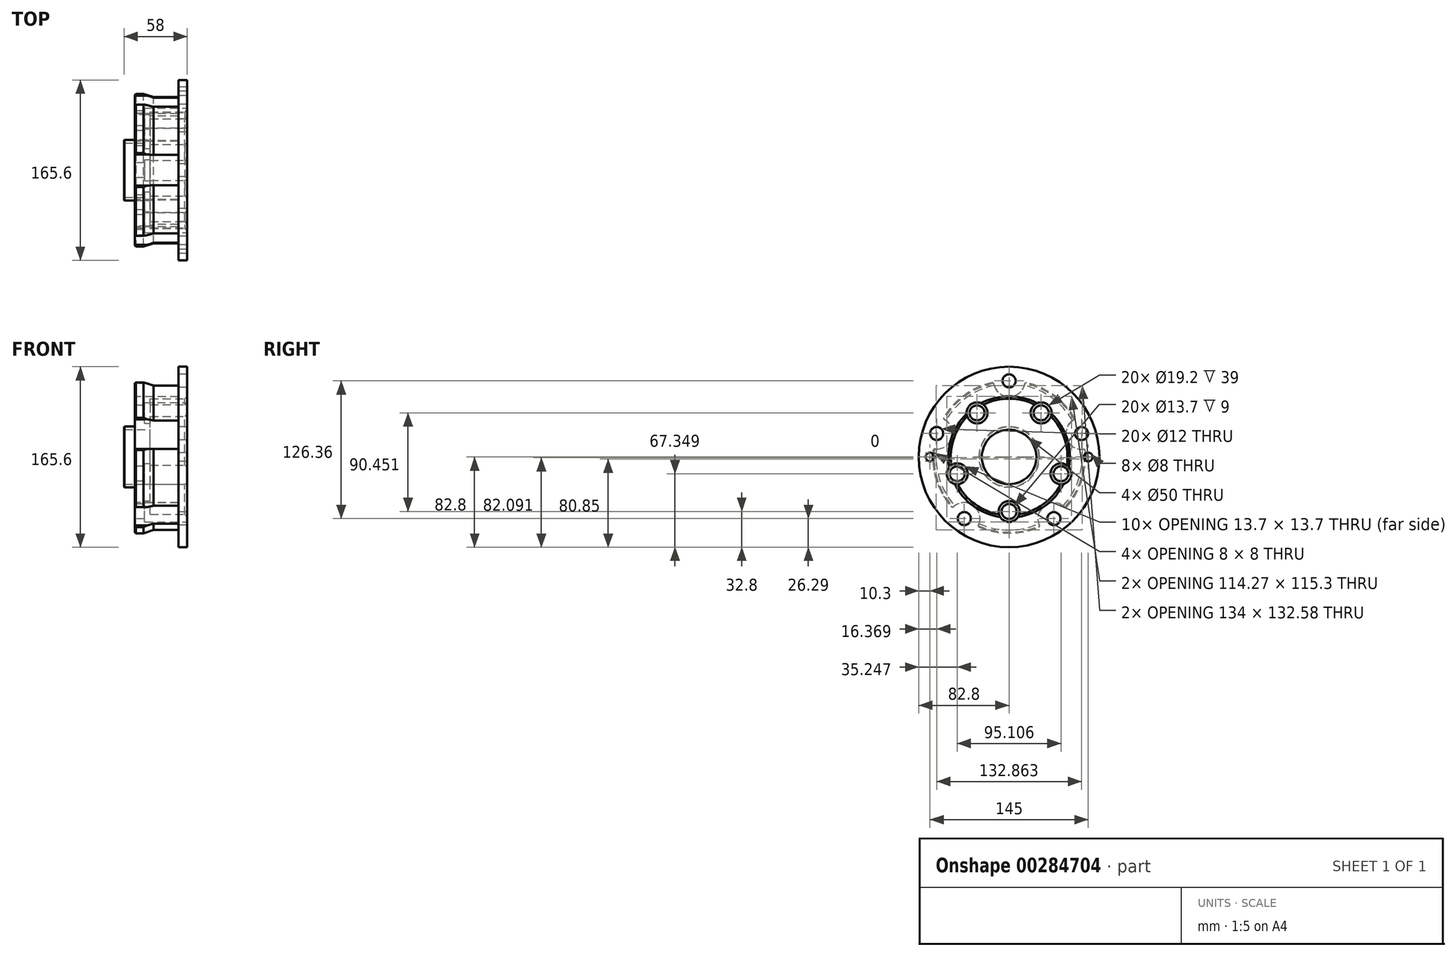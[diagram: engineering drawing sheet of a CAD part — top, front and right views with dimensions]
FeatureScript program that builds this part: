
annotation { "Feature Type Name" : "Feature", "Feature Type Description" : "" }
export const myFeature = defineFeature(function(context is Context, id is Id, definition is map)
    precondition{}
    {
        {
            var Q0;
            Q0=qCreatedBy(makeId("Front.planeOp"),FACE);
            var sketch = newSketch(context, id + "F0", { "sketchPlane" : qUnion([Q0])});
            skLineSegment(sketch, "E0", {"start": v(0, 0) * mm, "end": v(-58, 0) * mm});
            skLineSegment(sketch, "E1", {"start": v(0, 53.5) * mm, "end": v(0, 84.9) * mm});
            skLineSegment(sketch, "E2", {"start": v(0, 84.9) * mm, "end": v(-2.2, 84.9) * mm});
            skPoint(sketch, "E3", {"position": v(-2.2, 104) * mm});
            skLineSegment(sketch, "E4", {"start": v(-2.2, 84.9) * mm, "end": v(-2.2, 104) * mm});
            skLineSegment(sketch, "E5", {"start": v(-2.2, 104) * mm, "end": v(-10.2, 104) * mm});
            skPoint(sketch, "E6", {"position": v(-10.2, 67) * mm});
            skLineSegment(sketch, "E7", {"start": v(-10.2, 104) * mm, "end": v(-10.2, 67) * mm});
            skLineSegment(sketch, "E8", {"start": v(-10.2, 67) * mm, "end": v(-33.2, 67) * mm});
            skLineSegment(sketch, "E9", {"start": v(-33.2, 67) * mm, "end": v(-36.2, 67) * mm});
            skPoint(sketch, "E10", {"position": v(-50.2, 70) * mm});
            skLineSegment(sketch, "E11", {"start": v(-50.2, 70) * mm, "end": v(-50.2, 25) * mm});
            skPoint(sketch, "E12", {"position": v(0, 53.5) * mm});
            skLineSegment(sketch, "E13", {"start": v(0, 53.5) * mm, "end": v(-36.2, 53.5) * mm});
            skLineSegment(sketch, "E14", {"start": v(-36.2, 67) * mm, "end": v(-36.2, 0) * mm});
            skLineSegment(sketch, "E15", {"start": v(-36.2, 53.5) * mm, "end": v(-36.2, 25) * mm});
            skLineSegment(sketch, "E16", {"start": v(-50.2, 25) * mm, "end": v(-36.2, 25) * mm});
            skPoint(sketch, "E17.orphan", {"position": v(-36.2, 0) * mm});
            skPoint(sketch, "E18.orphan", {"position": v(-50.2, 0) * mm});
            skLineSegment(sketch, "E19", {"start": v(-50.2, 70) * mm, "end": v(-42.2, 70) * mm});
            skLineSegment(sketch, "E20", {"start": v(-42.2, 70) * mm, "end": v(-33.2, 67) * mm});
            skLineSegment(sketch, "E21", {"start": v(-2.2, 84.9) * mm, "end": v(-2.2, 53.5) * mm});
            skPoint(sketch, "E22", {"position": v(-2.2, 82.8) * mm});
            skLineSegment(sketch, "E23", {"start": v(-2.2, 82.8) * mm, "end": v(-10.2, 82.8) * mm});
            skLineSegment(sketch, "E24", {"start": v(-2.2, 82.8) * mm, "end": v(0, 82.8) * mm});
            skLineSegment(sketch, "E25", {"start": v(-50.2, 25) * mm, "end": v(-60.2, 25) * mm});
            skLineSegment(sketch, "E26", {"start": v(-60.2, 25) * mm, "end": v(-60.2, 27.85) * mm});
            skLineSegment(sketch, "E27", {"start": v(-60.2, 27.85) * mm, "end": v(-50.2, 27.85) * mm});
            skSolve(sketch);
        }
        {
            var Q0;
            Q0=qSketchRegion(id+"F0",true);
            var Q1;
            Q1=sQuery(id+"F0.wireOp",EDGE,"E0");
            revolve(context, id + "F1", {"entities" : qUnion([Q0]), "axis" : qUnion([Q1]), "revolveType" : RevolveType.FULL});
        }
        {
            var Q0;
            Q0=makeQuery(id+"F1.opRevolve","SWEPT_FACE",FACE,{"disambiguationData":[OSD([sQuery(id+"F0.wireOp",EDGE,"E11")])]});
            var sketch = newSketch(context, id + "F2", { "sketchPlane" : qUnion([Q0])});
            skCircle(sketch, "E28.0", {"center": v(0, 0) * mm, "radius": 70 * mm});
            skCircle(sketch, "E29", {"center": v(0, 0) * mm, "radius": 69.85 * mm, "construction": true});
            skLineSegment(sketch, "E30", {"start": v(0, 0) * mm, "end": v(0, 69.85) * mm});
            skCircle(sketch, "E31", {"center": v(0, 69.85) * mm, "radius": 6 * mm});
            skCircle(sketch, "E32.1.0", {"center": v(-66.43, 21.58) * mm, "radius": 6 * mm});
            skCircle(sketch, "E32.2.0", {"center": v(-41.06, -56.5) * mm, "radius": 6 * mm});
            skCircle(sketch, "E32.3.0", {"center": v(41.06, -56.5) * mm, "radius": 6 * mm});
            skCircle(sketch, "E32.4.0", {"center": v(66.43, 21.58) * mm, "radius": 6 * mm});
            skSolve(sketch);
        }
        {
            var Q0;
            {var subQ0=sQuery(id+"F2.wireOp",EDGE,"E31");var subQ1=makeQuery(id+"F1.opRevolve","SWEPT_EDGE",EDGE,{"disambiguationData":[OSD([sQuery(id+"F0.wireOp",EDGE,"E11"),sQuery(id+"F0.wireOp",EDGE,"E19")])]});var subQ2=makeQuery(id+"F2.imprint","INTERSECT",VERTEX,{"disambiguationData":[OD(0.0)],"derivedFrom":[subQ1,subQ0]});Q0=makeQuery(id+"F2.imprint","IMPRINT",FACE,{"disambiguationData":[TD([[makeQuery(id+"F2.imprint","IMPRINT",EDGE,{"disambiguationData":[TD([[subQ2,-1.0]])],"derivedFrom":subQ0}),1.0]])]});}
            var Q1;
            {var subQ0=sQuery(id+"F2.wireOp",EDGE,"E31");var subQ1=makeQuery(id+"F1.opRevolve","SWEPT_EDGE",EDGE,{"disambiguationData":[OSD([sQuery(id+"F0.wireOp",EDGE,"E11"),sQuery(id+"F0.wireOp",EDGE,"E19")])]});var subQ2=makeQuery(id+"F2.imprint","INTERSECT",VERTEX,{"disambiguationData":[OD(0.0)],"derivedFrom":[subQ1,subQ0]});Q1=makeQuery(id+"F2.imprint","IMPRINT",FACE,{"disambiguationData":[TD([[makeQuery(id+"F2.imprint","IMPRINT",EDGE,{"disambiguationData":[TD([[subQ2,1.0]])],"derivedFrom":subQ0}),1.0]])]});}
            var Q2;
            {var subQ0=sQuery(id+"F2.wireOp",EDGE,"E32.4.0");var subQ1=makeQuery(id+"F1.opRevolve","SWEPT_EDGE",EDGE,{"disambiguationData":[OSD([sQuery(id+"F0.wireOp",EDGE,"E11"),sQuery(id+"F0.wireOp",EDGE,"E19")])]});var subQ2=makeQuery(id+"F2.imprint","INTERSECT",VERTEX,{"disambiguationData":[OD(0.0)],"derivedFrom":[subQ1,subQ0]});Q2=makeQuery(id+"F2.imprint","IMPRINT",FACE,{"disambiguationData":[TD([[makeQuery(id+"F2.imprint","IMPRINT",EDGE,{"disambiguationData":[TD([[subQ2,-1.0]])],"derivedFrom":subQ0}),1.0]])]});}
            var Q3;
            {var subQ0=sQuery(id+"F2.wireOp",EDGE,"E32.4.0");var subQ1=makeQuery(id+"F1.opRevolve","SWEPT_EDGE",EDGE,{"disambiguationData":[OSD([sQuery(id+"F0.wireOp",EDGE,"E11"),sQuery(id+"F0.wireOp",EDGE,"E19")])]});var subQ2=makeQuery(id+"F2.imprint","INTERSECT",VERTEX,{"disambiguationData":[OD(0.0)],"derivedFrom":[subQ1,subQ0]});Q3=makeQuery(id+"F2.imprint","IMPRINT",FACE,{"disambiguationData":[TD([[makeQuery(id+"F2.imprint","IMPRINT",EDGE,{"disambiguationData":[TD([[subQ2,1.0]])],"derivedFrom":subQ0}),1.0]])]});}
            var Q4;
            {var subQ0=sQuery(id+"F2.wireOp",EDGE,"E32.3.0");var subQ1=makeQuery(id+"F1.opRevolve","SWEPT_EDGE",EDGE,{"disambiguationData":[OSD([sQuery(id+"F0.wireOp",EDGE,"E11"),sQuery(id+"F0.wireOp",EDGE,"E19")])]});var subQ2=makeQuery(id+"F2.imprint","INTERSECT",VERTEX,{"disambiguationData":[OD(0.0)],"derivedFrom":[subQ1,subQ0]});Q4=makeQuery(id+"F2.imprint","IMPRINT",FACE,{"disambiguationData":[TD([[makeQuery(id+"F2.imprint","IMPRINT",EDGE,{"disambiguationData":[TD([[subQ2,1.0]])],"derivedFrom":subQ0}),1.0]])]});}
            var Q5;
            {var subQ0=sQuery(id+"F2.wireOp",EDGE,"E32.3.0");var subQ1=makeQuery(id+"F1.opRevolve","SWEPT_EDGE",EDGE,{"disambiguationData":[OSD([sQuery(id+"F0.wireOp",EDGE,"E11"),sQuery(id+"F0.wireOp",EDGE,"E19")])]});var subQ2=makeQuery(id+"F2.imprint","INTERSECT",VERTEX,{"disambiguationData":[OD(0.0)],"derivedFrom":[subQ1,subQ0]});Q5=makeQuery(id+"F2.imprint","IMPRINT",FACE,{"disambiguationData":[TD([[makeQuery(id+"F2.imprint","IMPRINT",EDGE,{"disambiguationData":[TD([[subQ2,-1.0]])],"derivedFrom":subQ0}),1.0]])]});}
            var Q6;
            {var subQ0=sQuery(id+"F2.wireOp",EDGE,"E32.2.0");var subQ1=makeQuery(id+"F1.opRevolve","SWEPT_EDGE",EDGE,{"disambiguationData":[OSD([sQuery(id+"F0.wireOp",EDGE,"E11"),sQuery(id+"F0.wireOp",EDGE,"E19")])]});var subQ2=makeQuery(id+"F2.imprint","INTERSECT",VERTEX,{"disambiguationData":[OD(0.0)],"derivedFrom":[subQ1,subQ0]});Q6=makeQuery(id+"F2.imprint","IMPRINT",FACE,{"disambiguationData":[TD([[makeQuery(id+"F2.imprint","IMPRINT",EDGE,{"disambiguationData":[TD([[subQ2,1.0]])],"derivedFrom":subQ0}),1.0]])]});}
            var Q7;
            {var subQ0=sQuery(id+"F2.wireOp",EDGE,"E32.2.0");var subQ1=makeQuery(id+"F1.opRevolve","SWEPT_EDGE",EDGE,{"disambiguationData":[OSD([sQuery(id+"F0.wireOp",EDGE,"E11"),sQuery(id+"F0.wireOp",EDGE,"E19")])]});var subQ2=makeQuery(id+"F2.imprint","INTERSECT",VERTEX,{"disambiguationData":[OD(0.0)],"derivedFrom":[subQ1,subQ0]});Q7=makeQuery(id+"F2.imprint","IMPRINT",FACE,{"disambiguationData":[TD([[makeQuery(id+"F2.imprint","IMPRINT",EDGE,{"disambiguationData":[TD([[subQ2,-1.0]])],"derivedFrom":subQ0}),1.0]])]});}
            var Q8;
            {var subQ0=sQuery(id+"F2.wireOp",EDGE,"E32.1.0");var subQ1=makeQuery(id+"F1.opRevolve","SWEPT_EDGE",EDGE,{"disambiguationData":[OSD([sQuery(id+"F0.wireOp",EDGE,"E11"),sQuery(id+"F0.wireOp",EDGE,"E19")])]});var subQ2=makeQuery(id+"F2.imprint","INTERSECT",VERTEX,{"disambiguationData":[OD(0.0)],"derivedFrom":[subQ1,subQ0]});Q8=makeQuery(id+"F2.imprint","IMPRINT",FACE,{"disambiguationData":[TD([[makeQuery(id+"F2.imprint","IMPRINT",EDGE,{"disambiguationData":[TD([[subQ2,-1.0]])],"derivedFrom":subQ0}),1.0]])]});}
            var Q9;
            {var subQ0=sQuery(id+"F2.wireOp",EDGE,"E32.1.0");var subQ1=makeQuery(id+"F1.opRevolve","SWEPT_EDGE",EDGE,{"disambiguationData":[OSD([sQuery(id+"F0.wireOp",EDGE,"E11"),sQuery(id+"F0.wireOp",EDGE,"E19")])]});var subQ2=makeQuery(id+"F2.imprint","INTERSECT",VERTEX,{"disambiguationData":[OD(0.0)],"derivedFrom":[subQ1,subQ0]});Q9=makeQuery(id+"F2.imprint","IMPRINT",FACE,{"disambiguationData":[TD([[makeQuery(id+"F2.imprint","IMPRINT",EDGE,{"disambiguationData":[TD([[subQ2,1.0]])],"derivedFrom":subQ0}),1.0]])]});}
            extrude(context, id + "F3", {"entities" : qUnion([Q0, Q1, Q2, Q3, Q4, Q5, Q6, Q7, Q8, Q9]), "operationType" : NewBodyOperationType.REMOVE, "oppositeDirection" : true, "depth" : 48 * mm});
        }
        {
            var Q0;
            Q0=makeQuery(id+"F1.opRevolve","SWEPT_FACE",FACE,{"disambiguationData":[OSD([sQuery(id+"F0.wireOp",EDGE,"E11")])]});
            var sketch = newSketch(context, id + "F4", { "sketchPlane" : qUnion([Q0])});
            skCircle(sketch, "E33.0", {"center": v(0, 0) * mm, "radius": 25 * mm, "construction": true});
            skCircle(sketch, "E34", {"center": v(0, 0) * mm, "radius": 69.85 * mm, "construction": true});
            skPoint(sketch, "E35", {"position": v(-0.15, 69.85) * mm});
            skCircle(sketch, "E36", {"center": v(-0.15, 69.85) * mm, "radius": 14.5 * mm});
            skCircle(sketch, "E37.1.0", {"center": v(-66.48, 21.45) * mm, "radius": 14.5 * mm});
            skCircle(sketch, "E37.2.0", {"center": v(-40.94, -56.6) * mm, "radius": 14.5 * mm});
            skCircle(sketch, "E37.3.0", {"center": v(41.17, -56.42) * mm, "radius": 14.5 * mm});
            skCircle(sketch, "E37.4.0", {"center": v(66.39, 21.72) * mm, "radius": 14.5 * mm});
            skSolve(sketch);
        }
        {
            var Q0;
            Q0=qSketchRegion(id+"F4",true);
            extrude(context, id + "F5", {"entities" : qUnion([Q0]), "operationType" : NewBodyOperationType.REMOVE, "oppositeDirection" : true, "depth" : 40 * mm});
        }
        {
            var Q0;
            Q0=makeQuery(id+"F1.opRevolve","SWEPT_FACE",FACE,{"disambiguationData":[OSD([sQuery(id+"F0.wireOp",EDGE,"E11")])]});
            var sketch = newSketch(context, id + "F6", { "sketchPlane" : qUnion([Q0])});
            skCircle(sketch, "E38", {"center": v(0, 0) * mm, "radius": 50 * mm, "construction": true});
            skLineSegment(sketch, "E39", {"start": v(0, 0) * mm, "end": v(-29.39, 40.45) * mm});
            skCircle(sketch, "E40", {"center": v(-29.39, 40.45) * mm, "radius": 6.85 * mm});
            skCircle(sketch, "E41.1.0", {"center": v(-47.55, -15.45) * mm, "radius": 6.85 * mm});
            skCircle(sketch, "E41.2.0", {"center": v(0, -50) * mm, "radius": 6.85 * mm});
            skCircle(sketch, "E41.3.0", {"center": v(47.55, -15.45) * mm, "radius": 6.85 * mm});
            skCircle(sketch, "E41.4.0", {"center": v(29.39, 40.45) * mm, "radius": 6.85 * mm});
            skSolve(sketch);
        }
        {
            var Q0;
            Q0=qSketchRegion(id+"F6",true);
            extrude(context, id + "F7", {"entities" : qUnion([Q0]), "operationType" : NewBodyOperationType.REMOVE, "oppositeDirection" : true, "depth" : 14 * mm});
        }
        {
            var Q0;
            Q0=makeQuery(id+"F1.opRevolve","SWEPT_FACE",FACE,{"disambiguationData":[OSD([sQuery(id+"F0.wireOp",EDGE,"E1")])]});
            var sketch = newSketch(context, id + "F8", { "sketchPlane" : qUnion([Q0])});
            skCircle(sketch, "E42", {"center": v(0, 0) * mm, "radius": 50 * mm, "construction": true});
            skArc(sketch, "E43.0", {"start": v(-26.32, 46.58) * mm, "mid": v(-25.36, 34.9) * mm, "end": v(-36.16, 39.43) * mm, "construction": true});
            skCircle(sketch, "E44", {"center": v(-29.39, 40.45) * mm, "radius": 9.6 * mm});
            skCircle(sketch, "E45.1.0", {"center": v(-47.55, -15.45) * mm, "radius": 9.6 * mm});
            skCircle(sketch, "E45.2.0", {"center": v(0, -50) * mm, "radius": 9.6 * mm});
            skCircle(sketch, "E45.3.0", {"center": v(47.55, -15.45) * mm, "radius": 9.6 * mm});
            skCircle(sketch, "E45.4.0", {"center": v(29.39, 40.45) * mm, "radius": 9.6 * mm});
            skSolve(sketch);
        }
        {
            var Q0;
            Q0=qSketchRegion(id+"F8",true);
            extrude(context, id + "F9", {"entities" : qUnion([Q0]), "operationType" : NewBodyOperationType.REMOVE, "oppositeDirection" : true, "depth" : 41.2 * mm});
        }
        {
            var Q0;
            Q0=makeQuery(id+"F5.boolean.opBoolean","MERGE",FACE,{"derivedFrom":[makeQuery(id+"F1.opRevolve","SWEPT_FACE",FACE,{"disambiguationData":[OSD([sQuery(id+"F0.wireOp",EDGE,"E7")])]}),makeQuery(id+"F5.opExtrude","CAP_FACE",FACE,{"disambiguationData":[OSD([sQuery(id+"F4.wireOp",EDGE,"E36")])],"isStart":false}),makeQuery(id+"F5.opExtrude","CAP_FACE",FACE,{"disambiguationData":[OSD([sQuery(id+"F4.wireOp",EDGE,"E37.1.0")])],"isStart":false}),makeQuery(id+"F5.opExtrude","CAP_FACE",FACE,{"disambiguationData":[OSD([sQuery(id+"F4.wireOp",EDGE,"E37.2.0")])],"isStart":false}),makeQuery(id+"F5.opExtrude","CAP_FACE",FACE,{"disambiguationData":[OSD([sQuery(id+"F4.wireOp",EDGE,"E37.3.0")])],"isStart":false}),makeQuery(id+"F5.opExtrude","CAP_FACE",FACE,{"disambiguationData":[OSD([sQuery(id+"F4.wireOp",EDGE,"E37.4.0")])],"isStart":false})]});
            var sketch = newSketch(context, id + "F10", { "sketchPlane" : qUnion([Q0])});
            skLineSegment(sketch, "E46", {"start": v(0, 0) * mm, "end": v(-29.36, 90.35) * mm});
            skCircle(sketch, "E47", {"center": v(0, 0) * mm, "radius": 95 * mm, "construction": true});
            skCircle(sketch, "E48", {"center": v(-29.36, 90.35) * mm, "radius": 4 * mm});
            skCircle(sketch, "E49.1.0", {"center": v(-76.86, 55.84) * mm, "radius": 4 * mm});
            skCircle(sketch, "E49.2.0", {"center": v(-95, 0) * mm, "radius": 4 * mm});
            skCircle(sketch, "E49.3.0", {"center": v(-76.86, -55.84) * mm, "radius": 4 * mm});
            skCircle(sketch, "E49.4.0", {"center": v(-29.36, -90.35) * mm, "radius": 4 * mm});
            skCircle(sketch, "E49.5.0", {"center": v(29.36, -90.35) * mm, "radius": 4 * mm});
            skCircle(sketch, "E49.6.0", {"center": v(76.86, -55.84) * mm, "radius": 4 * mm});
            skCircle(sketch, "E49.7.0", {"center": v(95, 0) * mm, "radius": 4 * mm});
            skCircle(sketch, "E49.8.0", {"center": v(76.86, 55.84) * mm, "radius": 4 * mm});
            skCircle(sketch, "E49.9.0", {"center": v(29.36, 90.35) * mm, "radius": 4 * mm});
            skSolve(sketch);
        }
        {
            var Q0;
            Q0=qSketchRegion(id+"F10",true);
            extrude(context, id + "F11", {"entities" : qUnion([Q0]), "operationType" : NewBodyOperationType.REMOVE, "oppositeDirection" : true, "depth" : 8 * mm});
        }
        {
            var Q0;
            Q0=makeQuery(id+"F5.boolean.opBoolean","MERGE",FACE,{"derivedFrom":[makeQuery(id+"F1.opRevolve","SWEPT_FACE",FACE,{"disambiguationData":[OSD([sQuery(id+"F0.wireOp",EDGE,"E7")])]}),makeQuery(id+"F5.opExtrude","CAP_FACE",FACE,{"disambiguationData":[OSD([sQuery(id+"F4.wireOp",EDGE,"E36")])],"isStart":false}),makeQuery(id+"F5.opExtrude","CAP_FACE",FACE,{"disambiguationData":[OSD([sQuery(id+"F4.wireOp",EDGE,"E37.1.0")])],"isStart":false}),makeQuery(id+"F5.opExtrude","CAP_FACE",FACE,{"disambiguationData":[OSD([sQuery(id+"F4.wireOp",EDGE,"E37.2.0")])],"isStart":false}),makeQuery(id+"F5.opExtrude","CAP_FACE",FACE,{"disambiguationData":[OSD([sQuery(id+"F4.wireOp",EDGE,"E37.3.0")])],"isStart":false}),makeQuery(id+"F5.opExtrude","CAP_FACE",FACE,{"disambiguationData":[OSD([sQuery(id+"F4.wireOp",EDGE,"E37.4.0")])],"isStart":false})]});
            var sketch = newSketch(context, id + "F12", { "sketchPlane" : qUnion([Q0])});
            skCircle(sketch, "E50", {"center": v(0, 0) * mm, "radius": 95 * mm, "construction": true});
            skCircle(sketch, "E51.0", {"center": v(-29.36, 90.35) * mm, "radius": 4 * mm, "construction": true});
            skCircle(sketch, "E52", {"center": v(-29.36, 90.35) * mm, "radius": 7 * mm});
            skCircle(sketch, "E53.1.0", {"center": v(-76.86, 55.84) * mm, "radius": 7 * mm});
            skCircle(sketch, "E53.2.0", {"center": v(-95, 0) * mm, "radius": 7 * mm});
            skCircle(sketch, "E53.3.0", {"center": v(-76.86, -55.84) * mm, "radius": 7 * mm});
            skCircle(sketch, "E53.4.0", {"center": v(-29.36, -90.35) * mm, "radius": 7 * mm});
            skCircle(sketch, "E53.5.0", {"center": v(29.36, -90.35) * mm, "radius": 7 * mm});
            skCircle(sketch, "E53.6.0", {"center": v(76.86, -55.84) * mm, "radius": 7 * mm});
            skCircle(sketch, "E53.7.0", {"center": v(95, 0) * mm, "radius": 7 * mm});
            skCircle(sketch, "E53.8.0", {"center": v(76.86, 55.84) * mm, "radius": 7 * mm});
            skCircle(sketch, "E53.9.0", {"center": v(29.36, 90.35) * mm, "radius": 7 * mm});
            skSolve(sketch);
        }
        {
            var Q0;
            Q0=qSketchRegion(id+"F12",true);
            extrude(context, id + "F13", {"entities" : qUnion([Q0]), "operationType" : NewBodyOperationType.REMOVE, "oppositeDirection" : true, "depth" : 1 * mm});
        }
        {
            var Q0;
            {var subQ0=sQuery(id+"F0.wireOp",EDGE,"E1");var subQ1=sQuery(id+"F0.wireOp",EDGE,"E13");Q0=makeQuery(id+"F9.boolean.opBoolean","SPLIT",EDGE,{"disambiguationData":[TD([makeQuery(id+"F1.opRevolve","SWEPT_FACE",FACE,{"disambiguationData":[OSD([subQ0])]}),makeQuery(id+"F1.opRevolve","SWEPT_FACE",FACE,{"disambiguationData":[OSD([subQ1])]}),makeQuery(id+"F9.opExtrude","SWEPT_FACE",FACE,{"disambiguationData":[OSD([sQuery(id+"F8.wireOp",EDGE,"E44")])]}),makeQuery(id+"F9.opExtrude","SWEPT_FACE",FACE,{"disambiguationData":[OSD([sQuery(id+"F8.wireOp",EDGE,"E45.4.0")])]})])],"derivedFrom":makeQuery(id+"F1.opRevolve","SWEPT_EDGE",EDGE,{"disambiguationData":[OSD([subQ0,subQ1])]})});}
            var Q1;
            {var subQ0=sQuery(id+"F0.wireOp",EDGE,"E1");var subQ1=sQuery(id+"F0.wireOp",EDGE,"E13");Q1=makeQuery(id+"F9.boolean.opBoolean","SPLIT",EDGE,{"disambiguationData":[TD([makeQuery(id+"F1.opRevolve","SWEPT_FACE",FACE,{"disambiguationData":[OSD([subQ0])]}),makeQuery(id+"F1.opRevolve","SWEPT_FACE",FACE,{"disambiguationData":[OSD([subQ1])]}),makeQuery(id+"F9.opExtrude","SWEPT_FACE",FACE,{"disambiguationData":[OSD([sQuery(id+"F8.wireOp",EDGE,"E45.3.0")])]}),makeQuery(id+"F9.opExtrude","SWEPT_FACE",FACE,{"disambiguationData":[OSD([sQuery(id+"F8.wireOp",EDGE,"E45.4.0")])]})])],"derivedFrom":makeQuery(id+"F1.opRevolve","SWEPT_EDGE",EDGE,{"disambiguationData":[OSD([subQ0,subQ1])]})});}
            var Q2;
            {var subQ0=sQuery(id+"F0.wireOp",EDGE,"E1");var subQ1=sQuery(id+"F0.wireOp",EDGE,"E13");Q2=makeQuery(id+"F9.boolean.opBoolean","SPLIT",EDGE,{"disambiguationData":[TD([makeQuery(id+"F1.opRevolve","SWEPT_FACE",FACE,{"disambiguationData":[OSD([subQ0])]}),makeQuery(id+"F1.opRevolve","SWEPT_FACE",FACE,{"disambiguationData":[OSD([subQ1])]}),makeQuery(id+"F9.opExtrude","SWEPT_FACE",FACE,{"disambiguationData":[OSD([sQuery(id+"F8.wireOp",EDGE,"E45.2.0")])]}),makeQuery(id+"F9.opExtrude","SWEPT_FACE",FACE,{"disambiguationData":[OSD([sQuery(id+"F8.wireOp",EDGE,"E45.3.0")])]})])],"derivedFrom":makeQuery(id+"F1.opRevolve","SWEPT_EDGE",EDGE,{"disambiguationData":[OSD([subQ0,subQ1])]})});}
            var Q3;
            {var subQ0=sQuery(id+"F0.wireOp",EDGE,"E1");var subQ1=sQuery(id+"F0.wireOp",EDGE,"E13");Q3=makeQuery(id+"F9.boolean.opBoolean","SPLIT",EDGE,{"disambiguationData":[TD([makeQuery(id+"F1.opRevolve","SWEPT_FACE",FACE,{"disambiguationData":[OSD([subQ0])]}),makeQuery(id+"F1.opRevolve","SWEPT_FACE",FACE,{"disambiguationData":[OSD([subQ1])]}),makeQuery(id+"F9.opExtrude","SWEPT_FACE",FACE,{"disambiguationData":[OSD([sQuery(id+"F8.wireOp",EDGE,"E45.1.0")])]}),makeQuery(id+"F9.opExtrude","SWEPT_FACE",FACE,{"disambiguationData":[OSD([sQuery(id+"F8.wireOp",EDGE,"E45.2.0")])]})])],"derivedFrom":makeQuery(id+"F1.opRevolve","SWEPT_EDGE",EDGE,{"disambiguationData":[OSD([subQ0,subQ1])]})});}
            var Q4;
            {var subQ0=sQuery(id+"F0.wireOp",EDGE,"E1");var subQ1=sQuery(id+"F0.wireOp",EDGE,"E13");Q4=makeQuery(id+"F9.boolean.opBoolean","SPLIT",EDGE,{"disambiguationData":[TD([makeQuery(id+"F1.opRevolve","SWEPT_FACE",FACE,{"disambiguationData":[OSD([subQ0])]}),makeQuery(id+"F1.opRevolve","SWEPT_FACE",FACE,{"disambiguationData":[OSD([subQ1])]}),makeQuery(id+"F9.opExtrude","SWEPT_FACE",FACE,{"disambiguationData":[OSD([sQuery(id+"F8.wireOp",EDGE,"E44")])]}),makeQuery(id+"F9.opExtrude","SWEPT_FACE",FACE,{"disambiguationData":[OSD([sQuery(id+"F8.wireOp",EDGE,"E45.1.0")])]})])],"derivedFrom":makeQuery(id+"F1.opRevolve","SWEPT_EDGE",EDGE,{"disambiguationData":[OSD([subQ0,subQ1])]})});}
            chamfer(context, id + "F14", {"entities" : qUnion([Q0, Q1, Q2, Q3, Q4]), "width" : 2.2 * mm, "tangentPropagation" : true});
        }
        {
            var Q0;
            {var subQ0=sQuery(id+"F0.wireOp",EDGE,"E11");var subQ1=sQuery(id+"F0.wireOp",EDGE,"E19");Q0=makeQuery(id+"F3.boolean.opBoolean","SPLIT",EDGE,{"disambiguationData":[TD([makeQuery(id+"F1.opRevolve","SWEPT_FACE",FACE,{"disambiguationData":[OSD([subQ0])]}),makeQuery(id+"F1.opRevolve","SWEPT_FACE",FACE,{"disambiguationData":[OSD([subQ1])]}),makeQuery(id+"F3.opExtrude","SWEPT_FACE",FACE,{"disambiguationData":[OSD([sQuery(id+"F2.wireOp",EDGE,"isoNOGXv-9rzR-vXjO-d8jj-fEhT8795Os4k")])]}),makeQuery(id+"F3.opExtrude","SWEPT_FACE",FACE,{"disambiguationData":[OSD([sQuery(id+"F2.wireOp",EDGE,"ed49934d-06d9-406b-9f25-b05f826b0471.4.0")])]})])],"derivedFrom":makeQuery(id+"F1.opRevolve","SWEPT_EDGE",EDGE,{"disambiguationData":[OSD([subQ0,subQ1])]})});}
            var Q1;
            Q1=makeQuery(id+"F5.boolean.opBoolean","COPY",EDGE,{"derivedFrom":makeQuery(id+"F5.opExtrude","CAP_EDGE",EDGE,{"disambiguationData":[OSD([sQuery(id+"F4.wireOp",EDGE,"E37.4.0")])],"isStart":true})});
            var Q2;
            {var subQ0=sQuery(id+"F0.wireOp",EDGE,"E11");var subQ1=sQuery(id+"F0.wireOp",EDGE,"E19");Q2=makeQuery(id+"F3.boolean.opBoolean","SPLIT",EDGE,{"disambiguationData":[TD([makeQuery(id+"F1.opRevolve","SWEPT_FACE",FACE,{"disambiguationData":[OSD([subQ0])]}),makeQuery(id+"F1.opRevolve","SWEPT_FACE",FACE,{"disambiguationData":[OSD([subQ1])]}),makeQuery(id+"F3.opExtrude","SWEPT_FACE",FACE,{"disambiguationData":[OSD([sQuery(id+"F2.wireOp",EDGE,"ed49934d-06d9-406b-9f25-b05f826b0471.3.0")])]}),makeQuery(id+"F3.opExtrude","SWEPT_FACE",FACE,{"disambiguationData":[OSD([sQuery(id+"F2.wireOp",EDGE,"ed49934d-06d9-406b-9f25-b05f826b0471.4.0")])]})])],"derivedFrom":makeQuery(id+"F1.opRevolve","SWEPT_EDGE",EDGE,{"disambiguationData":[OSD([subQ0,subQ1])]})});}
            var Q3;
            Q3=makeQuery(id+"F5.boolean.opBoolean","COPY",EDGE,{"derivedFrom":makeQuery(id+"F5.opExtrude","CAP_EDGE",EDGE,{"disambiguationData":[OSD([sQuery(id+"F4.wireOp",EDGE,"E37.3.0")])],"isStart":true})});
            var Q4;
            {var subQ0=sQuery(id+"F0.wireOp",EDGE,"E11");var subQ1=sQuery(id+"F0.wireOp",EDGE,"E19");Q4=makeQuery(id+"F3.boolean.opBoolean","SPLIT",EDGE,{"disambiguationData":[TD([makeQuery(id+"F1.opRevolve","SWEPT_FACE",FACE,{"disambiguationData":[OSD([subQ0])]}),makeQuery(id+"F1.opRevolve","SWEPT_FACE",FACE,{"disambiguationData":[OSD([subQ1])]}),makeQuery(id+"F3.opExtrude","SWEPT_FACE",FACE,{"disambiguationData":[OSD([sQuery(id+"F2.wireOp",EDGE,"ed49934d-06d9-406b-9f25-b05f826b0471.2.0")])]}),makeQuery(id+"F3.opExtrude","SWEPT_FACE",FACE,{"disambiguationData":[OSD([sQuery(id+"F2.wireOp",EDGE,"ed49934d-06d9-406b-9f25-b05f826b0471.3.0")])]})])],"derivedFrom":makeQuery(id+"F1.opRevolve","SWEPT_EDGE",EDGE,{"disambiguationData":[OSD([subQ0,subQ1])]})});}
            var Q5;
            Q5=makeQuery(id+"F5.boolean.opBoolean","COPY",EDGE,{"derivedFrom":makeQuery(id+"F5.opExtrude","CAP_EDGE",EDGE,{"disambiguationData":[OSD([sQuery(id+"F4.wireOp",EDGE,"E37.2.0")])],"isStart":true})});
            var Q6;
            {var subQ0=sQuery(id+"F0.wireOp",EDGE,"E11");var subQ1=sQuery(id+"F0.wireOp",EDGE,"E19");Q6=makeQuery(id+"F3.boolean.opBoolean","SPLIT",EDGE,{"disambiguationData":[TD([makeQuery(id+"F1.opRevolve","SWEPT_FACE",FACE,{"disambiguationData":[OSD([subQ0])]}),makeQuery(id+"F1.opRevolve","SWEPT_FACE",FACE,{"disambiguationData":[OSD([subQ1])]}),makeQuery(id+"F3.opExtrude","SWEPT_FACE",FACE,{"disambiguationData":[OSD([sQuery(id+"F2.wireOp",EDGE,"ed49934d-06d9-406b-9f25-b05f826b0471.1.0")])]}),makeQuery(id+"F3.opExtrude","SWEPT_FACE",FACE,{"disambiguationData":[OSD([sQuery(id+"F2.wireOp",EDGE,"ed49934d-06d9-406b-9f25-b05f826b0471.2.0")])]})])],"derivedFrom":makeQuery(id+"F1.opRevolve","SWEPT_EDGE",EDGE,{"disambiguationData":[OSD([subQ0,subQ1])]})});}
            var Q7;
            Q7=makeQuery(id+"F5.boolean.opBoolean","COPY",EDGE,{"derivedFrom":makeQuery(id+"F5.opExtrude","CAP_EDGE",EDGE,{"disambiguationData":[OSD([sQuery(id+"F4.wireOp",EDGE,"E37.1.0")])],"isStart":true})});
            var Q8;
            {var subQ0=sQuery(id+"F0.wireOp",EDGE,"E11");var subQ1=sQuery(id+"F0.wireOp",EDGE,"E19");Q8=makeQuery(id+"F3.boolean.opBoolean","SPLIT",EDGE,{"disambiguationData":[TD([makeQuery(id+"F1.opRevolve","SWEPT_FACE",FACE,{"disambiguationData":[OSD([subQ0])]}),makeQuery(id+"F1.opRevolve","SWEPT_FACE",FACE,{"disambiguationData":[OSD([subQ1])]}),makeQuery(id+"F3.opExtrude","SWEPT_FACE",FACE,{"disambiguationData":[OSD([sQuery(id+"F2.wireOp",EDGE,"isoNOGXv-9rzR-vXjO-d8jj-fEhT8795Os4k")])]}),makeQuery(id+"F3.opExtrude","SWEPT_FACE",FACE,{"disambiguationData":[OSD([sQuery(id+"F2.wireOp",EDGE,"ed49934d-06d9-406b-9f25-b05f826b0471.1.0")])]})])],"derivedFrom":makeQuery(id+"F1.opRevolve","SWEPT_EDGE",EDGE,{"disambiguationData":[OSD([subQ0,subQ1])]})});}
            var Q9;
            Q9=makeQuery(id+"F5.boolean.opBoolean","COPY",EDGE,{"derivedFrom":makeQuery(id+"F5.opExtrude","CAP_EDGE",EDGE,{"disambiguationData":[OSD([sQuery(id+"F4.wireOp",EDGE,"E36")])],"isStart":true})});
            var Q10;
            Q10=makeQuery(id+"F5.boolean.opBoolean","INTERSECT",EDGE,{"derivedFrom":[makeQuery(id+"F3.boolean.opBoolean","SPLIT",FACE,{"disambiguationData":[TD([makeQuery(id+"F1.opRevolve","SWEPT_FACE",FACE,{"disambiguationData":[OSD([sQuery(id+"F0.wireOp",EDGE,"E11")])]}),makeQuery(id+"F1.opRevolve","SWEPT_FACE",FACE,{"disambiguationData":[OSD([sQuery(id+"F0.wireOp",EDGE,"E20")])]}),makeQuery(id+"F3.opExtrude","SWEPT_FACE",FACE,{"disambiguationData":[OSD([sQuery(id+"F2.wireOp",EDGE,"isoNOGXv-9rzR-vXjO-d8jj-fEhT8795Os4k")])]}),makeQuery(id+"F3.opExtrude","SWEPT_FACE",FACE,{"disambiguationData":[OSD([sQuery(id+"F2.wireOp",EDGE,"ed49934d-06d9-406b-9f25-b05f826b0471.4.0")])]})])],"derivedFrom":makeQuery(id+"F1.opRevolve","SWEPT_FACE",FACE,{"disambiguationData":[OSD([sQuery(id+"F0.wireOp",EDGE,"E19")])]})}),makeQuery(id+"F5.opExtrude","SWEPT_FACE",FACE,{"disambiguationData":[OSD([sQuery(id+"F4.wireOp",EDGE,"E36")])]})]});
            var Q11;
            Q11=makeQuery(id+"F5.boolean.opBoolean","INTERSECT",EDGE,{"derivedFrom":[makeQuery(id+"F3.boolean.opBoolean","SPLIT",FACE,{"disambiguationData":[TD([makeQuery(id+"F1.opRevolve","SWEPT_FACE",FACE,{"disambiguationData":[OSD([sQuery(id+"F0.wireOp",EDGE,"E11")])]}),makeQuery(id+"F1.opRevolve","SWEPT_FACE",FACE,{"disambiguationData":[OSD([sQuery(id+"F0.wireOp",EDGE,"E20")])]}),makeQuery(id+"F3.opExtrude","SWEPT_FACE",FACE,{"disambiguationData":[OSD([sQuery(id+"F2.wireOp",EDGE,"isoNOGXv-9rzR-vXjO-d8jj-fEhT8795Os4k")])]}),makeQuery(id+"F3.opExtrude","SWEPT_FACE",FACE,{"disambiguationData":[OSD([sQuery(id+"F2.wireOp",EDGE,"ed49934d-06d9-406b-9f25-b05f826b0471.1.0")])]})])],"derivedFrom":makeQuery(id+"F1.opRevolve","SWEPT_FACE",FACE,{"disambiguationData":[OSD([sQuery(id+"F0.wireOp",EDGE,"E19")])]})}),makeQuery(id+"F5.opExtrude","SWEPT_FACE",FACE,{"disambiguationData":[OSD([sQuery(id+"F4.wireOp",EDGE,"E36")])]})]});
            var Q12;
            Q12=makeQuery(id+"F5.boolean.opBoolean","INTERSECT",EDGE,{"derivedFrom":[makeQuery(id+"F3.boolean.opBoolean","SPLIT",FACE,{"disambiguationData":[TD([makeQuery(id+"F1.opRevolve","SWEPT_FACE",FACE,{"disambiguationData":[OSD([sQuery(id+"F0.wireOp",EDGE,"E11")])]}),makeQuery(id+"F1.opRevolve","SWEPT_FACE",FACE,{"disambiguationData":[OSD([sQuery(id+"F0.wireOp",EDGE,"E20")])]}),makeQuery(id+"F3.opExtrude","SWEPT_FACE",FACE,{"disambiguationData":[OSD([sQuery(id+"F2.wireOp",EDGE,"isoNOGXv-9rzR-vXjO-d8jj-fEhT8795Os4k")])]}),makeQuery(id+"F3.opExtrude","SWEPT_FACE",FACE,{"disambiguationData":[OSD([sQuery(id+"F2.wireOp",EDGE,"ed49934d-06d9-406b-9f25-b05f826b0471.4.0")])]})])],"derivedFrom":makeQuery(id+"F1.opRevolve","SWEPT_FACE",FACE,{"disambiguationData":[OSD([sQuery(id+"F0.wireOp",EDGE,"E19")])]})}),makeQuery(id+"F5.opExtrude","SWEPT_FACE",FACE,{"disambiguationData":[OSD([sQuery(id+"F4.wireOp",EDGE,"E37.4.0")])]})]});
            var Q13;
            Q13=makeQuery(id+"F5.boolean.opBoolean","INTERSECT",EDGE,{"derivedFrom":[makeQuery(id+"F3.boolean.opBoolean","SPLIT",FACE,{"disambiguationData":[TD([makeQuery(id+"F1.opRevolve","SWEPT_FACE",FACE,{"disambiguationData":[OSD([sQuery(id+"F0.wireOp",EDGE,"E11")])]}),makeQuery(id+"F1.opRevolve","SWEPT_FACE",FACE,{"disambiguationData":[OSD([sQuery(id+"F0.wireOp",EDGE,"E20")])]}),makeQuery(id+"F3.opExtrude","SWEPT_FACE",FACE,{"disambiguationData":[OSD([sQuery(id+"F2.wireOp",EDGE,"ed49934d-06d9-406b-9f25-b05f826b0471.3.0")])]}),makeQuery(id+"F3.opExtrude","SWEPT_FACE",FACE,{"disambiguationData":[OSD([sQuery(id+"F2.wireOp",EDGE,"ed49934d-06d9-406b-9f25-b05f826b0471.4.0")])]})])],"derivedFrom":makeQuery(id+"F1.opRevolve","SWEPT_FACE",FACE,{"disambiguationData":[OSD([sQuery(id+"F0.wireOp",EDGE,"E19")])]})}),makeQuery(id+"F5.opExtrude","SWEPT_FACE",FACE,{"disambiguationData":[OSD([sQuery(id+"F4.wireOp",EDGE,"E37.4.0")])]})]});
            var Q14;
            Q14=makeQuery(id+"F5.boolean.opBoolean","INTERSECT",EDGE,{"derivedFrom":[makeQuery(id+"F3.boolean.opBoolean","SPLIT",FACE,{"disambiguationData":[TD([makeQuery(id+"F1.opRevolve","SWEPT_FACE",FACE,{"disambiguationData":[OSD([sQuery(id+"F0.wireOp",EDGE,"E11")])]}),makeQuery(id+"F1.opRevolve","SWEPT_FACE",FACE,{"disambiguationData":[OSD([sQuery(id+"F0.wireOp",EDGE,"E20")])]}),makeQuery(id+"F3.opExtrude","SWEPT_FACE",FACE,{"disambiguationData":[OSD([sQuery(id+"F2.wireOp",EDGE,"ed49934d-06d9-406b-9f25-b05f826b0471.3.0")])]}),makeQuery(id+"F3.opExtrude","SWEPT_FACE",FACE,{"disambiguationData":[OSD([sQuery(id+"F2.wireOp",EDGE,"ed49934d-06d9-406b-9f25-b05f826b0471.4.0")])]})])],"derivedFrom":makeQuery(id+"F1.opRevolve","SWEPT_FACE",FACE,{"disambiguationData":[OSD([sQuery(id+"F0.wireOp",EDGE,"E19")])]})}),makeQuery(id+"F5.opExtrude","SWEPT_FACE",FACE,{"disambiguationData":[OSD([sQuery(id+"F4.wireOp",EDGE,"E37.3.0")])]})]});
            var Q15;
            Q15=makeQuery(id+"F5.boolean.opBoolean","INTERSECT",EDGE,{"derivedFrom":[makeQuery(id+"F3.boolean.opBoolean","SPLIT",FACE,{"disambiguationData":[TD([makeQuery(id+"F1.opRevolve","SWEPT_FACE",FACE,{"disambiguationData":[OSD([sQuery(id+"F0.wireOp",EDGE,"E11")])]}),makeQuery(id+"F1.opRevolve","SWEPT_FACE",FACE,{"disambiguationData":[OSD([sQuery(id+"F0.wireOp",EDGE,"E20")])]}),makeQuery(id+"F3.opExtrude","SWEPT_FACE",FACE,{"disambiguationData":[OSD([sQuery(id+"F2.wireOp",EDGE,"ed49934d-06d9-406b-9f25-b05f826b0471.2.0")])]}),makeQuery(id+"F3.opExtrude","SWEPT_FACE",FACE,{"disambiguationData":[OSD([sQuery(id+"F2.wireOp",EDGE,"ed49934d-06d9-406b-9f25-b05f826b0471.3.0")])]})])],"derivedFrom":makeQuery(id+"F1.opRevolve","SWEPT_FACE",FACE,{"disambiguationData":[OSD([sQuery(id+"F0.wireOp",EDGE,"E19")])]})}),makeQuery(id+"F5.opExtrude","SWEPT_FACE",FACE,{"disambiguationData":[OSD([sQuery(id+"F4.wireOp",EDGE,"E37.3.0")])]})]});
            var Q16;
            Q16=makeQuery(id+"F5.boolean.opBoolean","INTERSECT",EDGE,{"derivedFrom":[makeQuery(id+"F3.boolean.opBoolean","SPLIT",FACE,{"disambiguationData":[TD([makeQuery(id+"F1.opRevolve","SWEPT_FACE",FACE,{"disambiguationData":[OSD([sQuery(id+"F0.wireOp",EDGE,"E11")])]}),makeQuery(id+"F1.opRevolve","SWEPT_FACE",FACE,{"disambiguationData":[OSD([sQuery(id+"F0.wireOp",EDGE,"E20")])]}),makeQuery(id+"F3.opExtrude","SWEPT_FACE",FACE,{"disambiguationData":[OSD([sQuery(id+"F2.wireOp",EDGE,"ed49934d-06d9-406b-9f25-b05f826b0471.2.0")])]}),makeQuery(id+"F3.opExtrude","SWEPT_FACE",FACE,{"disambiguationData":[OSD([sQuery(id+"F2.wireOp",EDGE,"ed49934d-06d9-406b-9f25-b05f826b0471.3.0")])]})])],"derivedFrom":makeQuery(id+"F1.opRevolve","SWEPT_FACE",FACE,{"disambiguationData":[OSD([sQuery(id+"F0.wireOp",EDGE,"E19")])]})}),makeQuery(id+"F5.opExtrude","SWEPT_FACE",FACE,{"disambiguationData":[OSD([sQuery(id+"F4.wireOp",EDGE,"E37.2.0")])]})]});
            var Q17;
            Q17=makeQuery(id+"F5.boolean.opBoolean","INTERSECT",EDGE,{"derivedFrom":[makeQuery(id+"F3.boolean.opBoolean","SPLIT",FACE,{"disambiguationData":[TD([makeQuery(id+"F1.opRevolve","SWEPT_FACE",FACE,{"disambiguationData":[OSD([sQuery(id+"F0.wireOp",EDGE,"E11")])]}),makeQuery(id+"F1.opRevolve","SWEPT_FACE",FACE,{"disambiguationData":[OSD([sQuery(id+"F0.wireOp",EDGE,"E20")])]}),makeQuery(id+"F3.opExtrude","SWEPT_FACE",FACE,{"disambiguationData":[OSD([sQuery(id+"F2.wireOp",EDGE,"ed49934d-06d9-406b-9f25-b05f826b0471.1.0")])]}),makeQuery(id+"F3.opExtrude","SWEPT_FACE",FACE,{"disambiguationData":[OSD([sQuery(id+"F2.wireOp",EDGE,"ed49934d-06d9-406b-9f25-b05f826b0471.2.0")])]})])],"derivedFrom":makeQuery(id+"F1.opRevolve","SWEPT_FACE",FACE,{"disambiguationData":[OSD([sQuery(id+"F0.wireOp",EDGE,"E19")])]})}),makeQuery(id+"F5.opExtrude","SWEPT_FACE",FACE,{"disambiguationData":[OSD([sQuery(id+"F4.wireOp",EDGE,"E37.2.0")])]})]});
            var Q18;
            Q18=makeQuery(id+"F5.boolean.opBoolean","INTERSECT",EDGE,{"derivedFrom":[makeQuery(id+"F3.boolean.opBoolean","SPLIT",FACE,{"disambiguationData":[TD([makeQuery(id+"F1.opRevolve","SWEPT_FACE",FACE,{"disambiguationData":[OSD([sQuery(id+"F0.wireOp",EDGE,"E11")])]}),makeQuery(id+"F1.opRevolve","SWEPT_FACE",FACE,{"disambiguationData":[OSD([sQuery(id+"F0.wireOp",EDGE,"E20")])]}),makeQuery(id+"F3.opExtrude","SWEPT_FACE",FACE,{"disambiguationData":[OSD([sQuery(id+"F2.wireOp",EDGE,"ed49934d-06d9-406b-9f25-b05f826b0471.1.0")])]}),makeQuery(id+"F3.opExtrude","SWEPT_FACE",FACE,{"disambiguationData":[OSD([sQuery(id+"F2.wireOp",EDGE,"ed49934d-06d9-406b-9f25-b05f826b0471.2.0")])]})])],"derivedFrom":makeQuery(id+"F1.opRevolve","SWEPT_FACE",FACE,{"disambiguationData":[OSD([sQuery(id+"F0.wireOp",EDGE,"E19")])]})}),makeQuery(id+"F5.opExtrude","SWEPT_FACE",FACE,{"disambiguationData":[OSD([sQuery(id+"F4.wireOp",EDGE,"E37.1.0")])]})]});
            var Q19;
            Q19=makeQuery(id+"F5.boolean.opBoolean","INTERSECT",EDGE,{"derivedFrom":[makeQuery(id+"F3.boolean.opBoolean","SPLIT",FACE,{"disambiguationData":[TD([makeQuery(id+"F1.opRevolve","SWEPT_FACE",FACE,{"disambiguationData":[OSD([sQuery(id+"F0.wireOp",EDGE,"E11")])]}),makeQuery(id+"F1.opRevolve","SWEPT_FACE",FACE,{"disambiguationData":[OSD([sQuery(id+"F0.wireOp",EDGE,"E20")])]}),makeQuery(id+"F3.opExtrude","SWEPT_FACE",FACE,{"disambiguationData":[OSD([sQuery(id+"F2.wireOp",EDGE,"isoNOGXv-9rzR-vXjO-d8jj-fEhT8795Os4k")])]}),makeQuery(id+"F3.opExtrude","SWEPT_FACE",FACE,{"disambiguationData":[OSD([sQuery(id+"F2.wireOp",EDGE,"ed49934d-06d9-406b-9f25-b05f826b0471.1.0")])]})])],"derivedFrom":makeQuery(id+"F1.opRevolve","SWEPT_FACE",FACE,{"disambiguationData":[OSD([sQuery(id+"F0.wireOp",EDGE,"E19")])]})}),makeQuery(id+"F5.opExtrude","SWEPT_FACE",FACE,{"disambiguationData":[OSD([sQuery(id+"F4.wireOp",EDGE,"E37.1.0")])]})]});
            chamfer(context, id + "F15", {"entities" : qUnion([Q0, Q1, Q2, Q3, Q4, Q5, Q6, Q7, Q8, Q9, Q10, Q11, Q12, Q13, Q14, Q15, Q16, Q17, Q18, Q19]), "width" : 1 * mm, "tangentPropagation" : true});
        }
        {
            var Q0;
            Q0=makeQuery(id+"F5.boolean.opBoolean","MERGE",FACE,{"derivedFrom":[makeQuery(id+"F1.opRevolve","SWEPT_FACE",FACE,{"disambiguationData":[OSD([sQuery(id+"F0.wireOp",EDGE,"E7")])]}),makeQuery(id+"F5.opExtrude","CAP_FACE",FACE,{"disambiguationData":[OSD([sQuery(id+"F4.wireOp",EDGE,"E36")])],"isStart":false}),makeQuery(id+"F5.opExtrude","CAP_FACE",FACE,{"disambiguationData":[OSD([sQuery(id+"F4.wireOp",EDGE,"E37.1.0")])],"isStart":false}),makeQuery(id+"F5.opExtrude","CAP_FACE",FACE,{"disambiguationData":[OSD([sQuery(id+"F4.wireOp",EDGE,"E37.2.0")])],"isStart":false}),makeQuery(id+"F5.opExtrude","CAP_FACE",FACE,{"disambiguationData":[OSD([sQuery(id+"F4.wireOp",EDGE,"E37.3.0")])],"isStart":false}),makeQuery(id+"F5.opExtrude","CAP_FACE",FACE,{"disambiguationData":[OSD([sQuery(id+"F4.wireOp",EDGE,"E37.4.0")])],"isStart":false})]});
            var sketch = newSketch(context, id + "F16", { "sketchPlane" : qUnion([Q0])});
            skPoint(sketch, "E54", {"position": v(-72.5, 0) * mm});
            skPoint(sketch, "E55", {"position": v(72.5, 0) * mm});
            skCircle(sketch, "E56", {"center": v(-72.5, 0) * mm, "radius": 4 * mm});
            skCircle(sketch, "E57", {"center": v(72.5, 0) * mm, "radius": 4 * mm});
            skSolve(sketch);
        }
        {
            var Q0;
            Q0=qSketchRegion(id+"F16",true);
            extrude(context, id + "F17", {"entities" : qUnion([Q0]), "operationType" : NewBodyOperationType.REMOVE, "oppositeDirection" : true, "depth" : 10.22 * mm});
        }
        {
            var Q0;
            Q0=makeQuery(id+"F1.opRevolve","SWEPT_EDGE",EDGE,{"disambiguationData":[OSD([sQuery(id+"F0.wireOp",EDGE,"O30qBvRk-zJJW-lwZb-rN0x-yDuRLU4EX6qi"),sQuery(id+"F0.wireOp",EDGE,"kgTQcgjh-6w7j-LRSV-1dWs-DudFZEzoLzFv")])]});
            var Q1;
            Q1=makeQuery(id+"F1.opRevolve","SWEPT_EDGE",EDGE,{"disambiguationData":[OSD([sQuery(id+"F0.wireOp",EDGE,"WDxs43xY-JEfj-qPZn-62Lx-FkmzAmFiN1ub"),sQuery(id+"F0.wireOp",EDGE,"kgTQcgjh-6w7j-LRSV-1dWs-DudFZEzoLzFv")])]});
            var Q2;
            Q2=makeQuery(id+"F1.opRevolve","SWEPT_EDGE",EDGE,{"disambiguationData":[OSD([sQuery(id+"F0.wireOp",EDGE,"E5"),sQuery(id+"F0.wireOp",EDGE,"E7")])]});
            var Q3;
            Q3=makeQuery(id+"F1.opRevolve","SWEPT_EDGE",EDGE,{"disambiguationData":[OSD([sQuery(id+"F0.wireOp",EDGE,"E4"),sQuery(id+"F0.wireOp",EDGE,"E5")])]});
            chamfer(context, id + "F18", {"entities" : qUnion([Q0, Q1, Q2, Q3]), "width" : .5 * mm, "tangentPropagation" : true});
        }
        {
            var Q0;
            Q0=makeQuery(id+"F1.opRevolve","SWEPT_FACE",FACE,{"disambiguationData":[OSD([sQuery(id+"F0.wireOp",EDGE,"E1")])]});
            var sketch = newSketch(context, id + "F19", { "sketchPlane" : qUnion([Q0])});
            skCircle(sketch, "E58.0", {"center": v(0, 0) * mm, "radius": 84.9 * mm});
            skArc(sketch, "E59.0", {"start": v(23.52, 48.05) * mm, "mid": v(0, 53.5) * mm, "end": v(-23.52, 48.05) * mm});
            skSolve(sketch);
        }
        {
            var Q0;
            Q0=qSketchRegion(id+"F19",true);
            extrude(context, id + "F20", {"entities" : qUnion([Q0]), "operationType" : NewBodyOperationType.REMOVE, "oppositeDirection" : true, "depth" : 2.2 * mm});
        }
        {
            var Q0;
            Q0=makeQuery(id+"F20.boolean.opBoolean","MERGE",FACE,{"derivedFrom":[makeQuery(id+"F1.opRevolve","SWEPT_FACE",FACE,{"disambiguationData":[OSD([sQuery(id+"F0.wireOp",EDGE,"E4")])]}),makeQuery(id+"F20.opExtrude","CAP_FACE",FACE,{"disambiguationData":[OSD([sQuery(id+"F19.wireOp",EDGE,"E58.0")])],"isStart":false})]});
            var sketch = newSketch(context, id + "F21", { "sketchPlane" : qUnion([Q0])});
            skCircle(sketch, "E60.0", {"center": v(0, 0) * mm, "radius": 104 * mm});
            skCircle(sketch, "E61", {"center": v(0, 0) * mm, "radius": 82.8 * mm});
            skSolve(sketch);
        }
        {
            var Q0;
            Q0=qSketchRegion(id+"F21",true);
            extrude(context, id + "F22", {"entities" : qUnion([Q0]), "operationType" : NewBodyOperationType.REMOVE, "oppositeDirection" : true, "depth" : 8 * mm});
        }
        {
            var Q0;
            {var subQ0=sQuery(id+"F0.wireOp",EDGE,"E1");var subQ1=makeQuery(id+"F1.opRevolve","SWEPT_FACE",FACE,{"disambiguationData":[OSD([subQ0])]});var subQ2=makeQuery(id+"F9.opExtrude","SWEPT_FACE",FACE,{"disambiguationData":[OSD([sQuery(id+"F8.wireOp",EDGE,"E44")])]});var subQ3=makeQuery(id+"F9.opExtrude","SWEPT_FACE",FACE,{"disambiguationData":[OSD([sQuery(id+"F8.wireOp",EDGE,"E45.4.0")])]});var subQ4=sQuery(id+"F0.wireOp",EDGE,"E13");var subQ5=makeQuery(id+"F1.opRevolve","SWEPT_FACE",FACE,{"disambiguationData":[OSD([subQ4])]});Q0=makeQuery(id+"F14.opChamfer","BLEND_EDGE",EDGE,{"blendedFrom":[makeQuery(id+"F9.boolean.opBoolean","SPLIT",EDGE,{"disambiguationData":[TD([subQ1,subQ5,subQ2,subQ3])],"derivedFrom":makeQuery(id+"F1.opRevolve","SWEPT_EDGE",EDGE,{"disambiguationData":[OSD([subQ0,subQ4])]})}),makeQuery(id+"F9.boolean.opBoolean","SPLIT",FACE,{"disambiguationData":[TD([subQ1,makeQuery(id+"F1.opRevolve","SWEPT_FACE",FACE,{"disambiguationData":[OSD([sQuery(id+"F0.wireOp",EDGE,"E15")])]}),subQ2,subQ3])],"derivedFrom":subQ5})],"blendedInto":[makeQuery(id+"F9.boolean.opBoolean","SPLIT",FACE,{"disambiguationData":[TD([subQ1,makeQuery(id+"F1.opRevolve","SWEPT_FACE",FACE,{"disambiguationData":[OSD([sQuery(id+"F0.wireOp",EDGE,"E15")])]}),subQ2,subQ3])],"derivedFrom":subQ5})]});}
            var Q1;
            {var subQ0=sQuery(id+"F0.wireOp",EDGE,"E1");var subQ1=makeQuery(id+"F1.opRevolve","SWEPT_FACE",FACE,{"disambiguationData":[OSD([subQ0])]});var subQ2=makeQuery(id+"F9.opExtrude","SWEPT_FACE",FACE,{"disambiguationData":[OSD([sQuery(id+"F8.wireOp",EDGE,"E45.3.0")])]});var subQ3=makeQuery(id+"F9.opExtrude","SWEPT_FACE",FACE,{"disambiguationData":[OSD([sQuery(id+"F8.wireOp",EDGE,"E45.4.0")])]});var subQ4=sQuery(id+"F0.wireOp",EDGE,"E13");var subQ5=makeQuery(id+"F1.opRevolve","SWEPT_FACE",FACE,{"disambiguationData":[OSD([subQ4])]});Q1=makeQuery(id+"F14.opChamfer","BLEND_EDGE",EDGE,{"blendedFrom":[makeQuery(id+"F9.boolean.opBoolean","SPLIT",EDGE,{"disambiguationData":[TD([subQ1,subQ5,subQ2,subQ3])],"derivedFrom":makeQuery(id+"F1.opRevolve","SWEPT_EDGE",EDGE,{"disambiguationData":[OSD([subQ0,subQ4])]})}),makeQuery(id+"F9.boolean.opBoolean","SPLIT",FACE,{"disambiguationData":[TD([subQ1,makeQuery(id+"F1.opRevolve","SWEPT_FACE",FACE,{"disambiguationData":[OSD([sQuery(id+"F0.wireOp",EDGE,"E15")])]}),subQ2,subQ3])],"derivedFrom":subQ5})],"blendedInto":[makeQuery(id+"F9.boolean.opBoolean","SPLIT",FACE,{"disambiguationData":[TD([subQ1,makeQuery(id+"F1.opRevolve","SWEPT_FACE",FACE,{"disambiguationData":[OSD([sQuery(id+"F0.wireOp",EDGE,"E15")])]}),subQ2,subQ3])],"derivedFrom":subQ5})]});}
            var Q2;
            {var subQ0=sQuery(id+"F0.wireOp",EDGE,"E1");var subQ1=makeQuery(id+"F1.opRevolve","SWEPT_FACE",FACE,{"disambiguationData":[OSD([subQ0])]});var subQ2=makeQuery(id+"F9.opExtrude","SWEPT_FACE",FACE,{"disambiguationData":[OSD([sQuery(id+"F8.wireOp",EDGE,"E44")])]});var subQ3=makeQuery(id+"F9.opExtrude","SWEPT_FACE",FACE,{"disambiguationData":[OSD([sQuery(id+"F8.wireOp",EDGE,"E45.1.0")])]});var subQ4=sQuery(id+"F0.wireOp",EDGE,"E13");var subQ5=makeQuery(id+"F1.opRevolve","SWEPT_FACE",FACE,{"disambiguationData":[OSD([subQ4])]});Q2=makeQuery(id+"F14.opChamfer","BLEND_EDGE",EDGE,{"blendedFrom":[makeQuery(id+"F9.boolean.opBoolean","SPLIT",EDGE,{"disambiguationData":[TD([subQ1,subQ5,subQ2,subQ3])],"derivedFrom":makeQuery(id+"F1.opRevolve","SWEPT_EDGE",EDGE,{"disambiguationData":[OSD([subQ0,subQ4])]})}),makeQuery(id+"F9.boolean.opBoolean","SPLIT",FACE,{"disambiguationData":[TD([subQ1,makeQuery(id+"F1.opRevolve","SWEPT_FACE",FACE,{"disambiguationData":[OSD([sQuery(id+"F0.wireOp",EDGE,"E15")])]}),subQ2,subQ3])],"derivedFrom":subQ5})],"blendedInto":[makeQuery(id+"F9.boolean.opBoolean","SPLIT",FACE,{"disambiguationData":[TD([subQ1,makeQuery(id+"F1.opRevolve","SWEPT_FACE",FACE,{"disambiguationData":[OSD([sQuery(id+"F0.wireOp",EDGE,"E15")])]}),subQ2,subQ3])],"derivedFrom":subQ5})]});}
            var Q3;
            {var subQ0=sQuery(id+"F0.wireOp",EDGE,"E1");var subQ1=makeQuery(id+"F1.opRevolve","SWEPT_FACE",FACE,{"disambiguationData":[OSD([subQ0])]});var subQ2=makeQuery(id+"F9.opExtrude","SWEPT_FACE",FACE,{"disambiguationData":[OSD([sQuery(id+"F8.wireOp",EDGE,"E45.3.0")])]});var subQ3=makeQuery(id+"F9.opExtrude","SWEPT_FACE",FACE,{"disambiguationData":[OSD([sQuery(id+"F8.wireOp",EDGE,"E45.2.0")])]});var subQ4=sQuery(id+"F0.wireOp",EDGE,"E13");var subQ5=makeQuery(id+"F1.opRevolve","SWEPT_FACE",FACE,{"disambiguationData":[OSD([subQ4])]});Q3=makeQuery(id+"F14.opChamfer","BLEND_EDGE",EDGE,{"blendedFrom":[makeQuery(id+"F9.boolean.opBoolean","SPLIT",EDGE,{"disambiguationData":[TD([subQ1,subQ5,subQ3,subQ2])],"derivedFrom":makeQuery(id+"F1.opRevolve","SWEPT_EDGE",EDGE,{"disambiguationData":[OSD([subQ0,subQ4])]})}),makeQuery(id+"F9.boolean.opBoolean","SPLIT",FACE,{"disambiguationData":[TD([subQ1,makeQuery(id+"F1.opRevolve","SWEPT_FACE",FACE,{"disambiguationData":[OSD([sQuery(id+"F0.wireOp",EDGE,"E15")])]}),subQ3,subQ2])],"derivedFrom":subQ5})],"blendedInto":[makeQuery(id+"F9.boolean.opBoolean","SPLIT",FACE,{"disambiguationData":[TD([subQ1,makeQuery(id+"F1.opRevolve","SWEPT_FACE",FACE,{"disambiguationData":[OSD([sQuery(id+"F0.wireOp",EDGE,"E15")])]}),subQ3,subQ2])],"derivedFrom":subQ5})]});}
            var Q4;
            {var subQ0=sQuery(id+"F0.wireOp",EDGE,"E1");var subQ1=makeQuery(id+"F1.opRevolve","SWEPT_FACE",FACE,{"disambiguationData":[OSD([subQ0])]});var subQ2=makeQuery(id+"F9.opExtrude","SWEPT_FACE",FACE,{"disambiguationData":[OSD([sQuery(id+"F8.wireOp",EDGE,"E45.1.0")])]});var subQ3=makeQuery(id+"F9.opExtrude","SWEPT_FACE",FACE,{"disambiguationData":[OSD([sQuery(id+"F8.wireOp",EDGE,"E45.2.0")])]});var subQ4=sQuery(id+"F0.wireOp",EDGE,"E13");var subQ5=makeQuery(id+"F1.opRevolve","SWEPT_FACE",FACE,{"disambiguationData":[OSD([subQ4])]});Q4=makeQuery(id+"F14.opChamfer","BLEND_EDGE",EDGE,{"blendedFrom":[makeQuery(id+"F9.boolean.opBoolean","SPLIT",EDGE,{"disambiguationData":[TD([subQ1,subQ5,subQ2,subQ3])],"derivedFrom":makeQuery(id+"F1.opRevolve","SWEPT_EDGE",EDGE,{"disambiguationData":[OSD([subQ0,subQ4])]})}),makeQuery(id+"F9.boolean.opBoolean","SPLIT",FACE,{"disambiguationData":[TD([subQ1,makeQuery(id+"F1.opRevolve","SWEPT_FACE",FACE,{"disambiguationData":[OSD([sQuery(id+"F0.wireOp",EDGE,"E15")])]}),subQ2,subQ3])],"derivedFrom":subQ5})],"blendedInto":[makeQuery(id+"F9.boolean.opBoolean","SPLIT",FACE,{"disambiguationData":[TD([subQ1,makeQuery(id+"F1.opRevolve","SWEPT_FACE",FACE,{"disambiguationData":[OSD([sQuery(id+"F0.wireOp",EDGE,"E15")])]}),subQ2,subQ3])],"derivedFrom":subQ5})]});}
            chamfer(context, id + "F23", {"entities" : qUnion([Q0, Q1, Q2, Q3, Q4]), "width" : 2.2 * mm, "tangentPropagation" : true});
        }
        {
            var Q0;
            Q0=makeQuery(id+"F1.opRevolve","SWEPT_EDGE",EDGE,{"disambiguationData":[OSD([sQuery(id+"F0.wireOp",EDGE,"E25"),sQuery(id+"F0.wireOp",EDGE,"E26")])]});
            var Q1;
            Q1=makeQuery(id+"F1.opRevolve","SWEPT_EDGE",EDGE,{"disambiguationData":[OSD([sQuery(id+"F0.wireOp",EDGE,"E26"),sQuery(id+"F0.wireOp",EDGE,"E27")])]});
            var Q2;
            Q2=makeQuery(id+"F22.boolean.opBoolean","COPY",EDGE,{"derivedFrom":makeQuery(id+"F22.opExtrude","CAP_EDGE",EDGE,{"disambiguationData":[OSD([sQuery(id+"F21.wireOp",EDGE,"E61")])],"isStart":true})});
            var Q3;
            Q3=makeQuery(id+"F22.boolean.opBoolean","COPY",EDGE,{"derivedFrom":makeQuery(id+"F22.opExtrude","CAP_EDGE",EDGE,{"disambiguationData":[OSD([sQuery(id+"F21.wireOp",EDGE,"E61")])],"isStart":false})});
            chamfer(context, id + "F24", {"entities" : qUnion([Q0, Q1, Q2, Q3]), "width" : 0.5 * mm, "tangentPropagation" : true});
        }
    });
